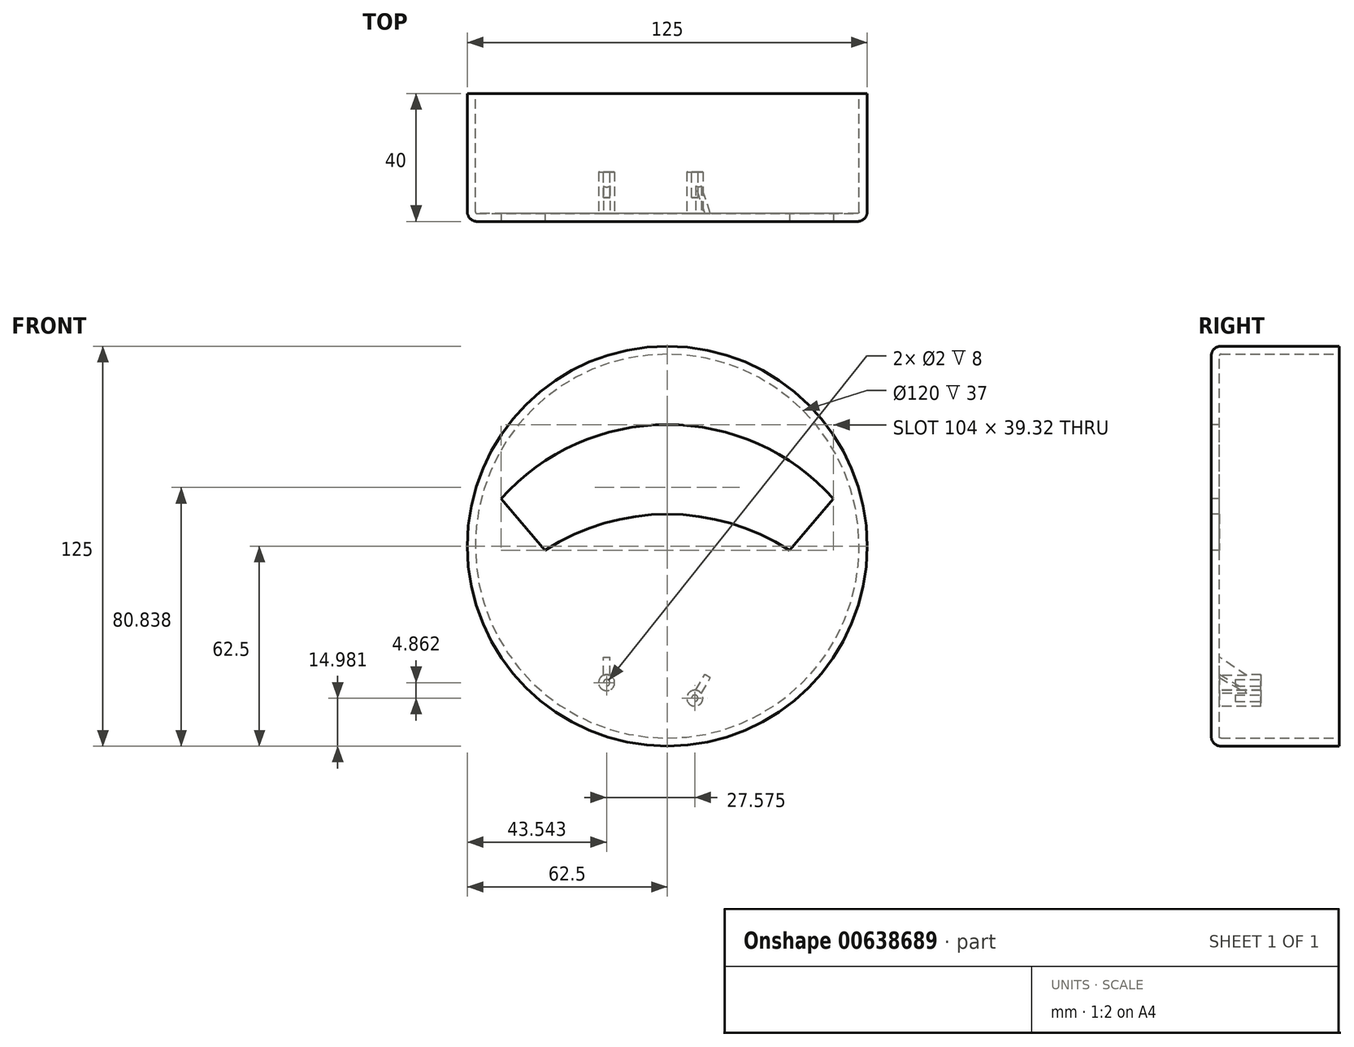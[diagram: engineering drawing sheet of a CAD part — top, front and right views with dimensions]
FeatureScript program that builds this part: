
annotation { "Feature Type Name" : "Feature", "Feature Type Description" : "" }
export const myFeature = defineFeature(function(context is Context, id is Id, definition is map)
    precondition{}
    {
        {
            var Q0;
            Q0=qCreatedBy(makeId("Front.planeOp"),FACE);
            var sketch = newSketch(context, id + "F0", { "sketchPlane" : qUnion([Q0])});
            skCircle(sketch, "E0", {"center": v(0, 0) * mm, "radius": 62.5 * mm});
            skSolve(sketch);
        }
        {
            var Q0;
            Q0 = qSketchRegion(id + "F0", true);
            extrude(context, id + "F1", {"entities" : qUnion([Q0]), "depth" : 40 * mm, "offsetDistance" : 25 * mm});
        }
        {
            var Q0;
            Q0=makeQuery(id+"F1.opExtrude","CAP_EDGE",EDGE,{"disambiguationData":[OSD([sQuery(id+"F0.wireOp",EDGE,"E0")])],"isStart":false});
            fillet(context, id + "F2", {"entities" : qUnion([Q0]), "radius" : 3 * mm, "tangentPropagation" : true, "allowEdgeOverflow" : false});
        }
        {
            var Q0;
            Q0=makeQuery(id+"F1.opExtrude","CAP_FACE",FACE,{"disambiguationData":[OSD([sQuery(id+"F0.wireOp",EDGE,"E0")])],"isStart":true});
            shell(context, id + "F3", {"entities" : qUnion([Q0]), "thickness" : 2.5 * mm});
        }
        {
            var Q0;
            Q0=makeQuery(id+"F1.opExtrude","CAP_FACE",FACE,{"disambiguationData":[OSD([sQuery(id+"F0.wireOp",EDGE,"E0")])],"isStart":false});
            var sketch = newSketch(context, id + "F4", { "sketchPlane" : qUnion([Q0])});
            skArc(sketch, "E1", {"start": v(-52, 14.86) * mm, "mid": v(0, 38) * mm, "end": v(52, 14.86) * mm});
            skArc(sketch, "E2", {"start": v(-38.17, -1.32) * mm, "mid": v(0, 10) * mm, "end": v(38.17, -1.32) * mm});
            skLineSegment(sketch, "E3", {"start": v(-52, 14.86) * mm, "end": v(-38.17, -1.32) * mm});
            skLineSegment(sketch, "E4", {"start": v(38.17, -1.32) * mm, "end": v(52, 14.86) * mm});
            skPoint(sketch, "E5", {"position": v(0, -46) * mm});
            skSolve(sketch);
        }
        {
            var Q0;
            Q0 = qSketchRegion(id + "F4", true);
            extrude(context, id + "F5", {"entities" : qUnion([Q0]), "operationType" : NewBodyOperationType.REMOVE, "endBound" : BoundingType.UP_TO_NEXT, "oppositeDirection" : true, "depth" : 25 * mm, "offsetDistance" : 25 * mm});
        }
        {
            var Q0;
            {var subQ0=sQuery(id+"F0.wireOp",EDGE,"E0");Q0=makeQuery(id+"F3.opShell","OFFSET_FACE",FACE,{"disambiguationData":[OSD([subQ0]),TDD([makeQuery(id+"F1.opExtrude","CAP_FACE",FACE,{"disambiguationData":[OSD([subQ0])],"isStart":false})])]});}
            var sketch = newSketch(context, id + "F6", { "sketchPlane" : qUnion([Q0])});
            skCircle(sketch, "E6", {"center": v(-8.62, -47.52) * mm, "radius": 2.5 * mm});
            skCircle(sketch, "E7", {"center": v(18.96, -42.66) * mm, "radius": 2.5 * mm});
            skLineSegment(sketch, "E8", {"start": v(-8.62, -47.52) * mm, "end": v(18.96, -42.66) * mm, "construction": true});
            skPoint(sketch, "E9.0", {"position": v(0, -46) * mm});
            skSolve(sketch);
        }
        {
            var Q0;
            Q0 = qSketchRegion(id + "F6", true);
            extrude(context, id + "F7", {"entities" : qUnion([Q0]), "operationType" : NewBodyOperationType.ADD, "depth" : 13 * mm, "offsetDistance" : 25 * mm});
        }
        {
            var Q0;
            Q0=makeQuery(id+"F7.opExtrude","CAP_FACE",FACE,{"disambiguationData":[OSD([sQuery(id+"F6.wireOp",EDGE,"E6")])],"isStart":false});
            var sketch = newSketch(context, id + "F8", { "sketchPlane" : qUnion([Q0])});
            skCircle(sketch, "E10", {"center": v(-8.62, -47.52) * mm, "radius": 1 * mm});
            skCircle(sketch, "E11.0", {"center": v(18.96, -42.66) * mm, "radius": 2.5 * mm, "construction": true});
            skCircle(sketch, "E12", {"center": v(18.96, -42.66) * mm, "radius": 1 * mm});
            skSolve(sketch);
        }
        {
            var Q0;
            Q0 = qSketchRegion(id + "F8", true);
            extrude(context, id + "F9", {"entities" : qUnion([Q0]), "operationType" : NewBodyOperationType.REMOVE, "oppositeDirection" : true, "depth" : 8 * mm, "offsetDistance" : 25 * mm});
        }
        {
            var Q0;
            Q0=makeQuery(id+"F9.boolean.opBoolean","COPY",FACE,{"derivedFrom":makeQuery(id+"F9.opExtrude","SWEPT_FACE",FACE,{"disambiguationData":[OSD([sQuery(id+"F8.wireOp",EDGE,"E10")])]})});
            var Q1;
            Q1=qCreatedBy(makeId("Right.planeOp"),FACE);
            cPlane(context, id + "F10", {"entities" : qUnion([Q0, Q1]), "cplaneType" : CPlaneType.LINE_ANGLE, "offset" : 25 * mm, "angle" : 330 * degree, "width" : 150 * mm, "height" : 150 * mm});
        }
        {
            var Q0;
            Q0=qCreatedBy(id+"F10.planeOp",FACE);
            var sketch = newSketch(context, id + "F11", { "sketchPlane" : qUnion([Q0])});
            skLineSegment(sketch, "E13", {"start": v(37.5, -34.84) * mm, "end": v(37.5, -28.84) * mm});
            skLineSegment(sketch, "E14", {"start": v(37.5, -28.84) * mm, "end": v(28.5, -34.84) * mm});
            skLineSegment(sketch, "E15", {"start": v(37.5, -34.84) * mm, "end": v(28.5, -34.84) * mm});
            skLineSegment(sketch, "E16.0", {"start": v(37.5, -39.34) * mm, "end": v(37.5, -34.34) * mm, "construction": true});
            skSolve(sketch);
        }
        {
            var Q0;
            Q0 = qSketchRegion(id + "F11", true);
            extrude(context, id + "F12", {"entities" : qUnion([Q0]), "operationType" : NewBodyOperationType.ADD, "endBound" : BoundingType.SYMMETRIC, "depth" : 2 * mm, "offsetDistance" : 25 * mm});
        }
        {
            var Q0;
            Q0=makeQuery(id+"F9.boolean.opBoolean","COPY",FACE,{"derivedFrom":makeQuery(id+"F9.opExtrude","SWEPT_FACE",FACE,{"disambiguationData":[OSD([sQuery(id+"F8.wireOp",EDGE,"E12")])]})});
            var Q1;
            Q1=qCreatedBy(makeId("Right.planeOp"),FACE);
            cPlane(context, id + "F13", {"entities" : qUnion([Q0, Q1]), "cplaneType" : CPlaneType.LINE_ANGLE, "offset" : 25 * mm, "angle" : 0 * degree, "width" : 150 * mm, "height" : 150 * mm});
        }
        {
            var Q0;
            Q0=qCreatedBy(id+"F13.planeOp",FACE);
            var sketch = newSketch(context, id + "F14", { "sketchPlane" : qUnion([Q0])});
            skLineSegment(sketch, "E17.0", {"start": v(37.5, -45.16) * mm, "end": v(37.5, -40.16) * mm});
            skLineSegment(sketch, "E18", {"start": v(37.5, -40.66) * mm, "end": v(28.5, -40.66) * mm});
            skLineSegment(sketch, "E19", {"start": v(28.5, -40.66) * mm, "end": v(37.5, -34.66) * mm});
            skLineSegment(sketch, "E20", {"start": v(37.5, -34.66) * mm, "end": v(37.5, -40.66) * mm});
            skSolve(sketch);
        }
        {
            var Q0;
            Q0 = qSketchRegion(id + "F14", true);
            extrude(context, id + "F15", {"entities" : qUnion([Q0]), "operationType" : NewBodyOperationType.ADD, "depth" : 1 * mm, "offsetDistance" : 25 * mm, "hasSecondDirection" : true, "secondDirectionOppositeDirection" : true, "secondDirectionDepth" : 1 * mm});
        }
    });
